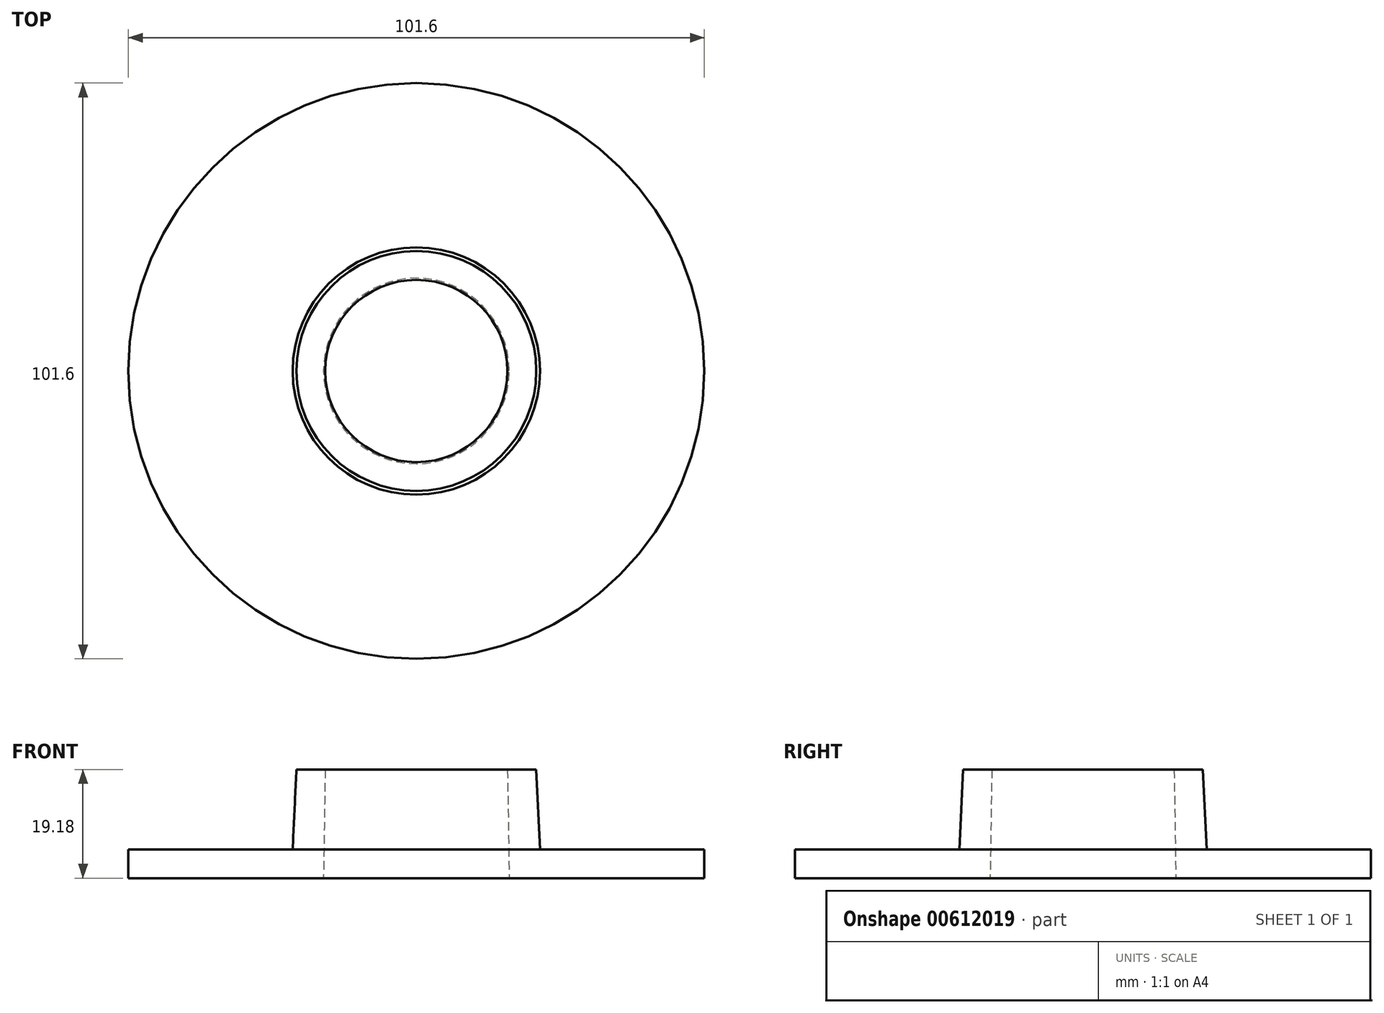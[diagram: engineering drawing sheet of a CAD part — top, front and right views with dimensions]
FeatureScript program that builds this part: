
annotation { "Feature Type Name" : "Feature", "Feature Type Description" : "" }
export const myFeature = defineFeature(function(context is Context, id is Id, definition is map)
    precondition{}
    {
        {
            var Q0;
            Q0=qCreatedBy(makeId("Front.planeOp"),FACE);
            var sketch = newSketch(context, id + "F0", { "sketchPlane" : qUnion([Q0])});
            skLineSegment(sketch, "E0", {"start": v(0, 0) * mm, "end": v(0, 19.1) * mm, "construction": true});
            skLineSegment(sketch, "E1", {"start": v(0, 19.1) * mm, "end": v(-16.08, 19.1) * mm, "construction": true});
            skLineSegment(sketch, "E2", {"start": v(0, 0) * mm, "end": v(-16.38, 0) * mm, "construction": true});
            skLineSegment(sketch, "E3", {"start": v(-16.38, 0) * mm, "end": v(-50.8, 0) * mm});
            skLineSegment(sketch, "E4", {"start": v(-50.8, 0) * mm, "end": v(-50.8, 5.09) * mm});
            skLineSegment(sketch, "E5", {"start": v(-50.8, 5.09) * mm, "end": v(-21.82, 5.09) * mm});
            skLineSegment(sketch, "E6", {"start": v(-16.38, 0) * mm, "end": v(-16.08, 19.1) * mm});
            skLineSegment(sketch, "E7", {"start": v(-16.08, 19.1) * mm, "end": v(-21.16, 19.18) * mm});
            skLineSegment(sketch, "E8", {"start": v(-21.16, 19.18) * mm, "end": v(-21.82, 5.09) * mm});
            skSolve(sketch);
        }
        {
            var Q0;
            Q0=makeQuery(id+"F0.imprint","IMPRINT",FACE,{"disambiguationData":[TD([[makeQuery(id+"F0.imprint","IMPRINT",EDGE,{"derivedFrom":sQuery(id+"F0.wireOp",EDGE,"E3")}),-1.0]])]});
            var Q1;
            Q1=sQuery(id+"F0.wireOp",EDGE,"E0");
            revolve(context, id + "F1", {"entities" : qUnion([Q0]), "axis" : qUnion([Q1]), "revolveType" : RevolveType.FULL});
        }
    });
